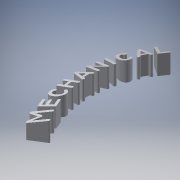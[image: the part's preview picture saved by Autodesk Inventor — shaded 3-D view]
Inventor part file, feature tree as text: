
AUTODESK INVENTOR PART (.ipt)
format: ipt  version: 2016 (Build 200138000, 138)  size: 784,896 bytes
history: native  units: in
note: dims shown in document units (in); Inventor stores cm internally (conversion verified against a paired STEP export)
features: projected_geometry x12, sketch x4, extrude x3, revolve x1, plane x1, pattern_circular x1
ambient origin geometry x8: Origin, YZ Plane, XZ Plane, XY Plane, X Axis, Y Axis, Z Axis, Center Point
bodies: Solid1 (feature_tree)
feature tree (22):
  revolve  "Revolution1"  [1 undecoded]
  plane  "Work Plane1"
  extrude  "Extrusion1"  Depth=0.1in
  pattern_circular  "Circular Pattern1"  Angle=90.0deg  [1 undecoded]
  extrude  "Extrusion2"  Depth=0.1in
  extrude  "Extrusion3"  Depth=0.35in
  sketch  "Sketch1"  dims[d0=0.8265in d1=0.175in]
  sketch  "Sketch2"  dims[d2=0.05in d3=0.1in]
  sketch  "Sketch3"  dims[d4=0.15in]
  projected_geometry  "Projected Loop1"
  projected_geometry  "Projected Loop2"
  sketch  "Sketch4"  dims[d5=0.275in d6=90.0deg d7=0.1in d8=0.35in d9=0.2in d10=0.1in d11=1.0in d12=0.0in d13=4.7244in d14=360.0deg d16=0.075in d17=1.0in d18=0.0in d19=0.0197in d20=0.0in]
  projected_geometry  "Projected Loop3"
  projected_geometry  "Projected Loop4"
  projected_geometry  "Projected Loop5"
  projected_geometry  "Projected Loop6"
  projected_geometry  "Projected Loop7"
  projected_geometry  "Projected Loop8"
  projected_geometry  "Projected Loop9"
  projected_geometry  "Projected Loop10"
  projected_geometry  "Projected Loop11"
  projected_geometry  "Projected Loop12"
note: 2 required parameter values undecoded (feature->parameter linkage not recoverable at this tier; creation-order binding heuristic only, values carry confidence <= 0.55)